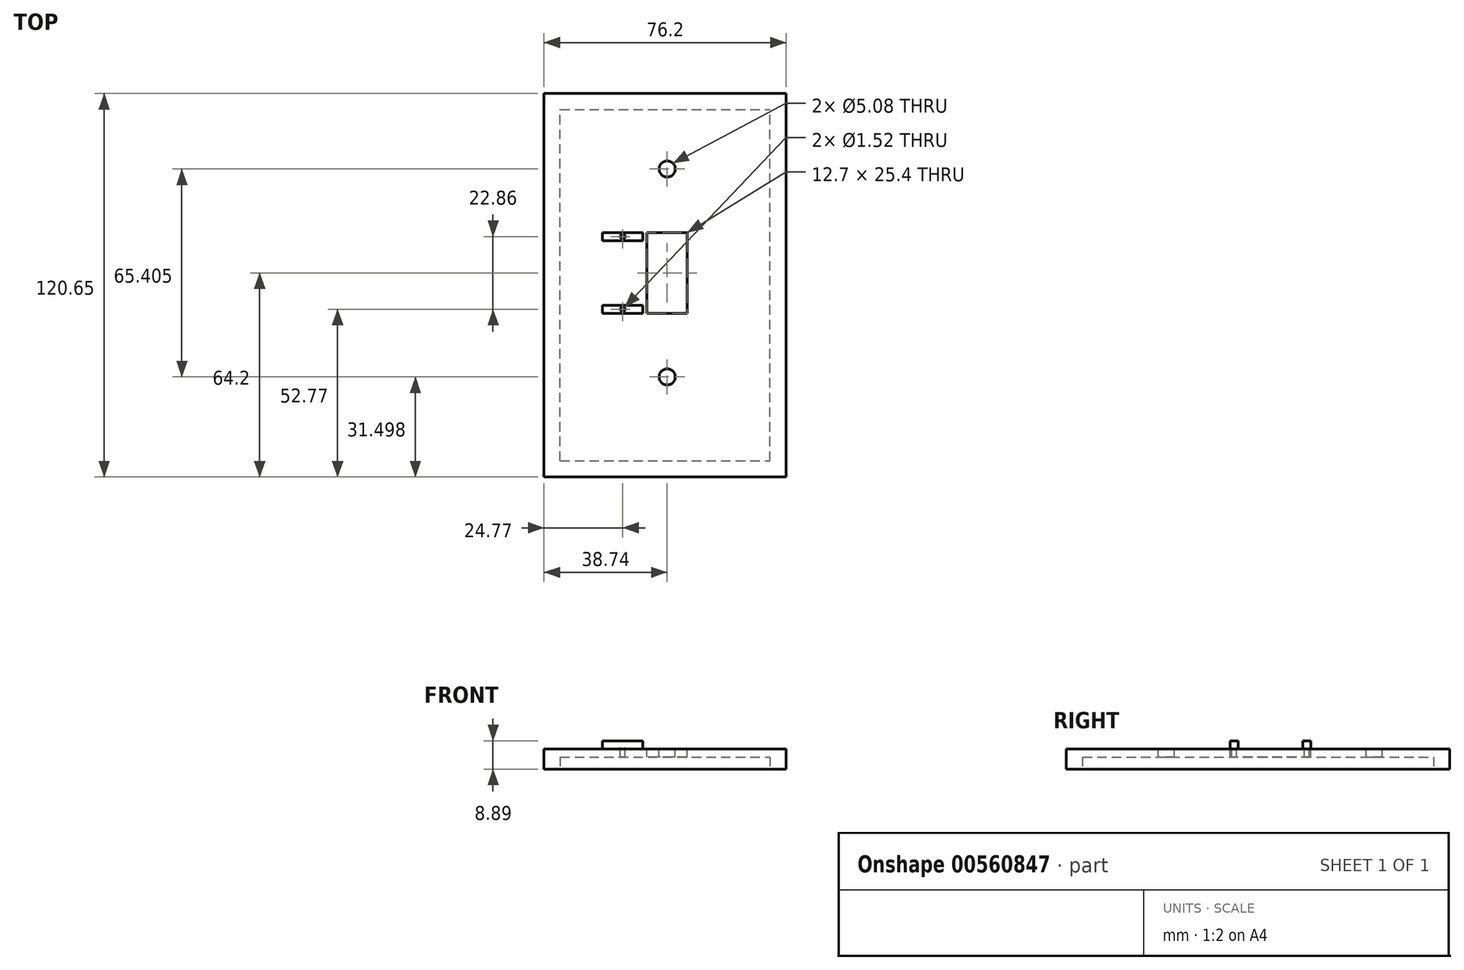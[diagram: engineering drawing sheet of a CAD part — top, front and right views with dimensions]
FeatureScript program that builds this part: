
annotation { "Feature Type Name" : "Feature", "Feature Type Description" : "" }
export const myFeature = defineFeature(function(context is Context, id is Id, definition is map)
    precondition{}
    {
        {
            var Q0;
            Q0=qCreatedBy(makeId("Top.planeOp"),FACE);
            var sketch = newSketch(context, id + "F0", { "sketchPlane" : qUnion([Q0])});
            skLineSegment(sketch, "E0.bottom", {"start": v(-38.74, 56.45) * mm, "end": v(37.46, 56.45) * mm});
            skLineSegment(sketch, "E0.top", {"start": v(-38.74, -64.2) * mm, "end": v(37.46, -64.2) * mm});
            skLineSegment(sketch, "E0.left", {"start": v(-38.74, 56.45) * mm, "end": v(-38.74, -64.2) * mm});
            skLineSegment(sketch, "E0.right", {"start": v(37.46, 56.45) * mm, "end": v(37.46, -64.2) * mm});
            skSolve(sketch);
        }
        {
            var Q0;
            Q0=makeQuery(id+"F0.imprint","IMPRINT",FACE,{"disambiguationData":[TD([[makeQuery(id+"F0.imprint","IMPRINT",EDGE,{"derivedFrom":sQuery(id+"F0.wireOp",EDGE,"E0.bottom")}),-1.0]])]});
            extrude(context, id + "F1", {"entities" : qUnion([Q0]), "depth" : 6.35 * mm, "offsetDistance" : 25.4 * mm});
        }
        {
            var Q0;
            Q0=makeQuery(id+"F1.opExtrude","CAP_FACE",FACE,{"disambiguationData":[OSD([sQuery(id+"F0.wireOp",EDGE,"E0.bottom"),sQuery(id+"F0.wireOp",EDGE,"E0.top"),sQuery(id+"F0.wireOp",EDGE,"E0.left"),sQuery(id+"F0.wireOp",EDGE,"E0.right")])],"isStart":false});
            var sketch = newSketch(context, id + "F2", { "sketchPlane" : qUnion([Q0])});
            skLineSegment(sketch, "E1.bottom", {"start": v(6.35, 12.7) * mm, "end": v(-6.35, 12.7) * mm});
            skLineSegment(sketch, "E1.top", {"start": v(6.35, -12.7) * mm, "end": v(-6.35, -12.7) * mm});
            skLineSegment(sketch, "E1.left", {"start": v(6.35, 12.7) * mm, "end": v(6.35, -12.7) * mm});
            skLineSegment(sketch, "E1.right", {"start": v(-6.35, 12.7) * mm, "end": v(-6.35, -12.7) * mm});
            skPoint(sketch, "E1.middle", {"position": v(0, 0) * mm});
            skSolve(sketch);
        }
        {
            var Q0;
            Q0=makeQuery(id+"F2.imprint","IMPRINT",FACE,{"disambiguationData":[TD([[makeQuery(id+"F2.imprint","IMPRINT",EDGE,{"derivedFrom":sQuery(id+"F2.wireOp",EDGE,"E1.bottom")}),1.0]])]});
            extrude(context, id + "F3", {"entities" : qUnion([Q0]), "operationType" : NewBodyOperationType.REMOVE, "oppositeDirection" : true, "depth" : 6.35 * mm, "offsetDistance" : 25.4 * mm});
        }
        {
            var Q0;
            Q0=makeQuery(id+"F1.opExtrude","CAP_FACE",FACE,{"disambiguationData":[OSD([sQuery(id+"F0.wireOp",EDGE,"E0.bottom"),sQuery(id+"F0.wireOp",EDGE,"E0.top"),sQuery(id+"F0.wireOp",EDGE,"E0.left"),sQuery(id+"F0.wireOp",EDGE,"E0.right")])],"isStart":false});
            var sketch = newSketch(context, id + "F4", { "sketchPlane" : qUnion([Q0])});
            skCircle(sketch, "E2", {"center": v(0, 32.7) * mm, "radius": 2.54 * mm});
            skCircle(sketch, "E3", {"center": v(0, -32.7) * mm, "radius": 2.54 * mm});
            skSolve(sketch);
        }
        {
            var Q0;
            Q0=makeQuery(id+"F4.imprint","IMPRINT",FACE,{"disambiguationData":[TD([[makeQuery(id+"F4.imprint","IMPRINT",EDGE,{"derivedFrom":sQuery(id+"F4.wireOp",EDGE,"E3")}),1.0]])]});
            var Q1;
            Q1=makeQuery(id+"F4.imprint","IMPRINT",FACE,{"disambiguationData":[TD([[makeQuery(id+"F4.imprint","IMPRINT",EDGE,{"derivedFrom":sQuery(id+"F4.wireOp",EDGE,"E2")}),1.0]])]});
            extrude(context, id + "F5", {"entities" : qUnion([Q0, Q1]), "operationType" : NewBodyOperationType.REMOVE, "oppositeDirection" : true, "depth" : 6.35 * mm, "offsetDistance" : 25.4 * mm});
        }
        {
            var Q0;
            Q0=makeQuery(id+"F1.opExtrude","CAP_FACE",FACE,{"disambiguationData":[OSD([sQuery(id+"F0.wireOp",EDGE,"E0.bottom"),sQuery(id+"F0.wireOp",EDGE,"E0.top"),sQuery(id+"F0.wireOp",EDGE,"E0.left"),sQuery(id+"F0.wireOp",EDGE,"E0.right")])],"isStart":false});
            var sketch = newSketch(context, id + "F6", { "sketchPlane" : qUnion([Q0])});
            skLineSegment(sketch, "E4.bottom", {"start": v(-7.62, 12.7) * mm, "end": v(-20.32, 12.7) * mm});
            skLineSegment(sketch, "E4.top", {"start": v(-7.62, -12.7) * mm, "end": v(-20.32, -12.7) * mm});
            skLineSegment(sketch, "E4.left", {"start": v(-7.62, 12.7) * mm, "end": v(-7.62, -12.7) * mm});
            skLineSegment(sketch, "E4.right", {"start": v(-20.32, 12.7) * mm, "end": v(-20.32, -12.7) * mm});
            skPoint(sketch, "E4.middle", {"position": v(-13.97, 0) * mm});
            skLineSegment(sketch, "E5", {"start": v(-20.32, 10.16) * mm, "end": v(-7.62, 10.16) * mm});
            skLineSegment(sketch, "E6", {"start": v(-20.32, -10.16) * mm, "end": v(-7.62, -10.16) * mm});
            skSolve(sketch);
        }
        {
            var Q0;
            {var subQ0=sQuery(id+"F6.wireOp",EDGE,"E4.bottom");Q0=makeQuery(id+"F6.imprint","IMPRINT",FACE,{"disambiguationData":[TD([[makeQuery(id+"F6.imprint","IMPRINT",EDGE,{"derivedFrom":subQ0}),1.0]])]});}
            var Q1;
            {var subQ0=sQuery(id+"F6.wireOp",EDGE,"E4.top");Q1=makeQuery(id+"F6.imprint","IMPRINT",FACE,{"disambiguationData":[TD([[makeQuery(id+"F6.imprint","IMPRINT",EDGE,{"derivedFrom":subQ0}),-1.0]])]});}
            extrude(context, id + "F7", {"entities" : qUnion([Q0, Q1]), "operationType" : NewBodyOperationType.ADD, "depth" : 2.54 * mm, "offsetDistance" : 25.4 * mm});
        }
        {
            var Q0;
            Q0=makeQuery(id+"F7.opExtrude","CAP_FACE",FACE,{"disambiguationData":[OSD([sQuery(id+"F6.wireOp",EDGE,"E4.bottom"),sQuery(id+"F6.wireOp",EDGE,"E4.left"),sQuery(id+"F6.wireOp",EDGE,"E4.right"),sQuery(id+"F6.wireOp",EDGE,"E5")])],"isStart":false});
            var sketch = newSketch(context, id + "F8", { "sketchPlane" : qUnion([Q0])});
            skCircle(sketch, "E7", {"center": v(-13.97, 11.43) * mm, "radius": 0.76 * mm});
            skPoint(sketch, "E7.centerSnap0", {"position": v(-20.32, 11.43) * mm});
            skSolve(sketch);
        }
        {
            var Q0;
            Q0=makeQuery(id+"F7.opExtrude","CAP_FACE",FACE,{"disambiguationData":[OSD([sQuery(id+"F6.wireOp",EDGE,"E4.top"),sQuery(id+"F6.wireOp",EDGE,"E4.left"),sQuery(id+"F6.wireOp",EDGE,"E4.right"),sQuery(id+"F6.wireOp",EDGE,"E6")])],"isStart":false});
            var sketch = newSketch(context, id + "F9", { "sketchPlane" : qUnion([Q0])});
            skCircle(sketch, "E8", {"center": v(-13.97, -11.43) * mm, "radius": 0.76 * mm});
            skPoint(sketch, "E8.centerSnap0", {"position": v(-20.32, -11.43) * mm});
            skPoint(sketch, "E8.centerSnap1", {"position": v(-13.97, -12.7) * mm});
            skSolve(sketch);
        }
        {
            var Q0;
            Q0=makeQuery(id+"F8.imprint","IMPRINT",FACE,{"disambiguationData":[TD([[makeQuery(id+"F8.imprint","IMPRINT",EDGE,{"derivedFrom":sQuery(id+"F8.wireOp",EDGE,"E7")}),1.0]])]});
            var Q1;
            Q1=makeQuery(id+"F9.imprint","IMPRINT",FACE,{"disambiguationData":[TD([[makeQuery(id+"F9.imprint","IMPRINT",EDGE,{"derivedFrom":sQuery(id+"F9.wireOp",EDGE,"E8")}),1.0]])]});
            extrude(context, id + "F10", {"entities" : qUnion([Q0, Q1]), "operationType" : NewBodyOperationType.REMOVE, "oppositeDirection" : true, "depth" : 11.94 * mm, "offsetDistance" : 25.4 * mm});
        }
        {
            var Q0;
            Q0=makeQuery(id+"F1.opExtrude","CAP_FACE",FACE,{"disambiguationData":[OSD([sQuery(id+"F0.wireOp",EDGE,"E0.bottom"),sQuery(id+"F0.wireOp",EDGE,"E0.top"),sQuery(id+"F0.wireOp",EDGE,"E0.left"),sQuery(id+"F0.wireOp",EDGE,"E0.right")])],"isStart":true});
            var sketch = newSketch(context, id + "F11", { "sketchPlane" : qUnion([Q0])});
            skLineSegment(sketch, "E9.bottom", {"start": v(-33.66, 59.12) * mm, "end": v(32.38, 59.12) * mm});
            skLineSegment(sketch, "E9.top", {"start": v(-33.66, -51.37) * mm, "end": v(32.38, -51.37) * mm});
            skLineSegment(sketch, "E9.left", {"start": v(-33.66, 59.12) * mm, "end": v(-33.66, -51.37) * mm});
            skLineSegment(sketch, "E9.right", {"start": v(32.38, 59.12) * mm, "end": v(32.38, -51.37) * mm});
            skSolve(sketch);
        }
        {
            var Q0;
            Q0=makeQuery(id+"F11.imprint","IMPRINT",FACE,{"disambiguationData":[TD([[makeQuery(id+"F11.imprint","IMPRINT",EDGE,{"derivedFrom":sQuery(id+"F11.wireOp",EDGE,"E9.bottom")}),-1.0]])]});
            extrude(context, id + "F12", {"entities" : qUnion([Q0]), "operationType" : NewBodyOperationType.REMOVE, "oppositeDirection" : true, "depth" : 3.8 * mm, "offsetDistance" : 25.4 * mm});
        }
    });
